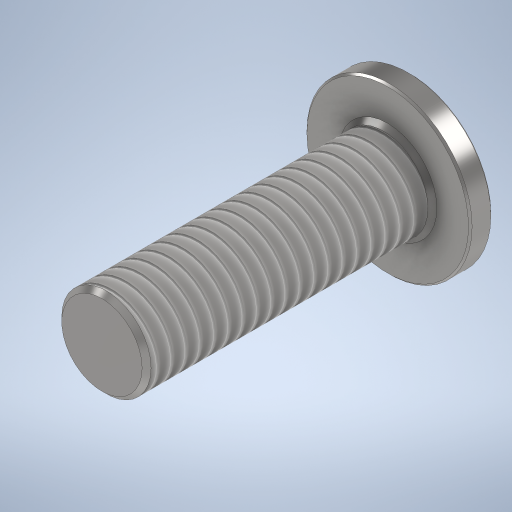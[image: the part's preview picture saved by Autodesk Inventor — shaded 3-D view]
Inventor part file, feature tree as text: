
AUTODESK INVENTOR PART (.ipt)
format: ipt  version: 2024 (Build 280153000, 153)  size: 368,640 bytes
history: native  units: mm
features: extrude x3, chamfer x3, sketch x2, thread x1, hole x1
ambient origin geometry x8: Origin, YZ Plane, XZ Plane, XY Plane, X Axis, Y Axis, Z Axis, Center Point
bodies: Solid1 (feature_tree)
feature tree (10):
  sketch  "Sketch1"  dims[d0=9.25mm d1=5.0mm]
  extrude  "Extrusion1"  Depth=5.0mm
  extrude  "Extrusion2"  Depth=2.5mm TaperAngle=0.0deg
  thread  "Thread1"  [1 undecoded]
  chamfer  "Chamfer1"  Distance=0.1mm Angle=45.0deg
  sketch  "Sketch2"  dims[d2=16.0mm d3=0.0mm d4=1.25mm d5=0.0mm d6=15.0mm d7=0.0mm d8=0.1mm d9=2.0mm d10=45.0deg d11=3.75mm d15=0.5mm d16=0.8mm d17=45.0deg d18=3.0mm d19=0.0mm d20=0.25mm d21=2.0mm d22=45.0deg d23=2.5mm d24=6.0mm d25=4.0mm d26=2.0mm d27=90.0deg d28=2.5mm d29=150.0deg d30=3.94mm d31=0.66mm d32=1.66mm d33=2.5mm]
  hole  "Hole1"  [1 undecoded]
  chamfer  "Chamfer2"  Distance=3.0mm
  extrude  "Extrusion4"  Depth=2.5mm TaperAngle=45.0deg
  chamfer  "Chamfer3"  Distance=2.5mm
note: 2 required parameter values undecoded (feature->parameter linkage not recoverable at this tier; creation-order binding heuristic only, values carry confidence <= 0.55)
